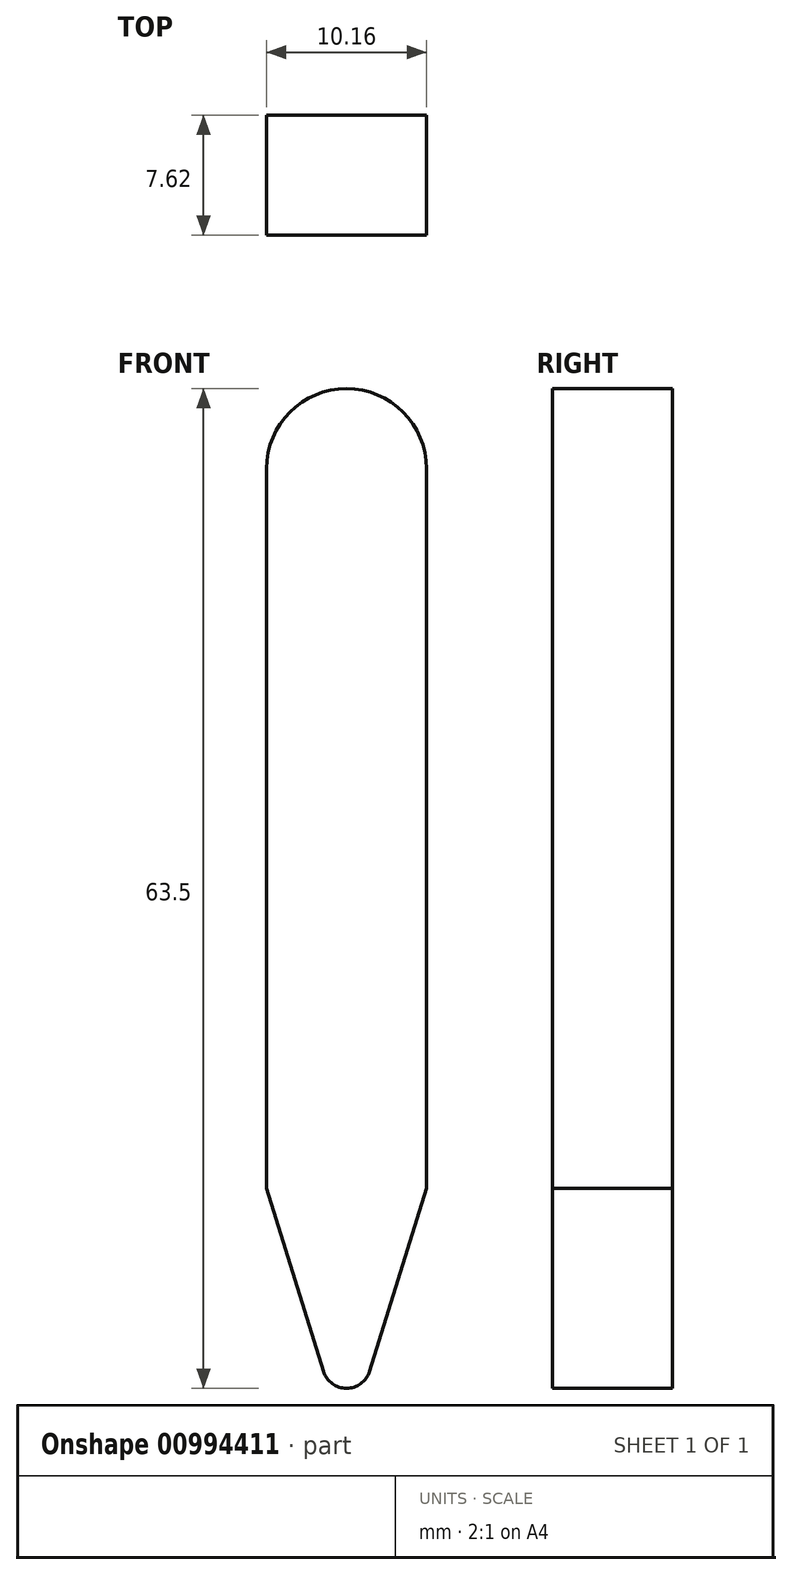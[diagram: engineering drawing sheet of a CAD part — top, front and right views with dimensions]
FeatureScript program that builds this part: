
annotation { "Feature Type Name" : "Feature", "Feature Type Description" : "" }
export const myFeature = defineFeature(function(context is Context, id is Id, definition is map)
    precondition{}
    {
        {
            var Q0;
            Q0=qCreatedBy(makeId("Front.planeOp"),FACE);
            var sketch = newSketch(context, id + "F0", { "sketchPlane" : qUnion([Q0])});
            skLineSegment(sketch, "E0.bottom", {"start": v(5.08, -22.86) * mm, "end": v(-5.08, -22.86) * mm});
            skLineSegment(sketch, "E0.top", {"start": v(5.08, 22.86) * mm, "end": v(-5.08, 22.86) * mm});
            skLineSegment(sketch, "E0.left", {"start": v(5.08, -22.86) * mm, "end": v(5.08, 22.86) * mm});
            skLineSegment(sketch, "E0.right", {"start": v(-5.08, -22.86) * mm, "end": v(-5.08, 22.86) * mm});
            skPoint(sketch, "E0.middle", {"position": v(0, 0) * mm});
            skArc(sketch, "E1", {"start": v(5.08, 22.86) * mm, "mid": v(0, 27.94) * mm, "end": v(-5.08, 22.86) * mm});
            skCircle(sketch, "E2", {"center": v(0, -34.04) * mm, "radius": 1.52 * mm});
            skLineSegment(sketch, "E3", {"start": v(-5.08, -22.86) * mm, "end": v(-1.45, -34.49) * mm});
            skLineSegment(sketch, "E4", {"start": v(5.08, -22.86) * mm, "end": v(1.45, -34.49) * mm});
            skSolve(sketch);
        }
        {
            var Q0;
            Q0 = qSketchRegion(id + "F0", true);
            extrude(context, id + "F1", {"entities" : qUnion([Q0]), "depth" : 7.62 * mm, "offsetDistance" : 25.4 * mm});
        }
    });
